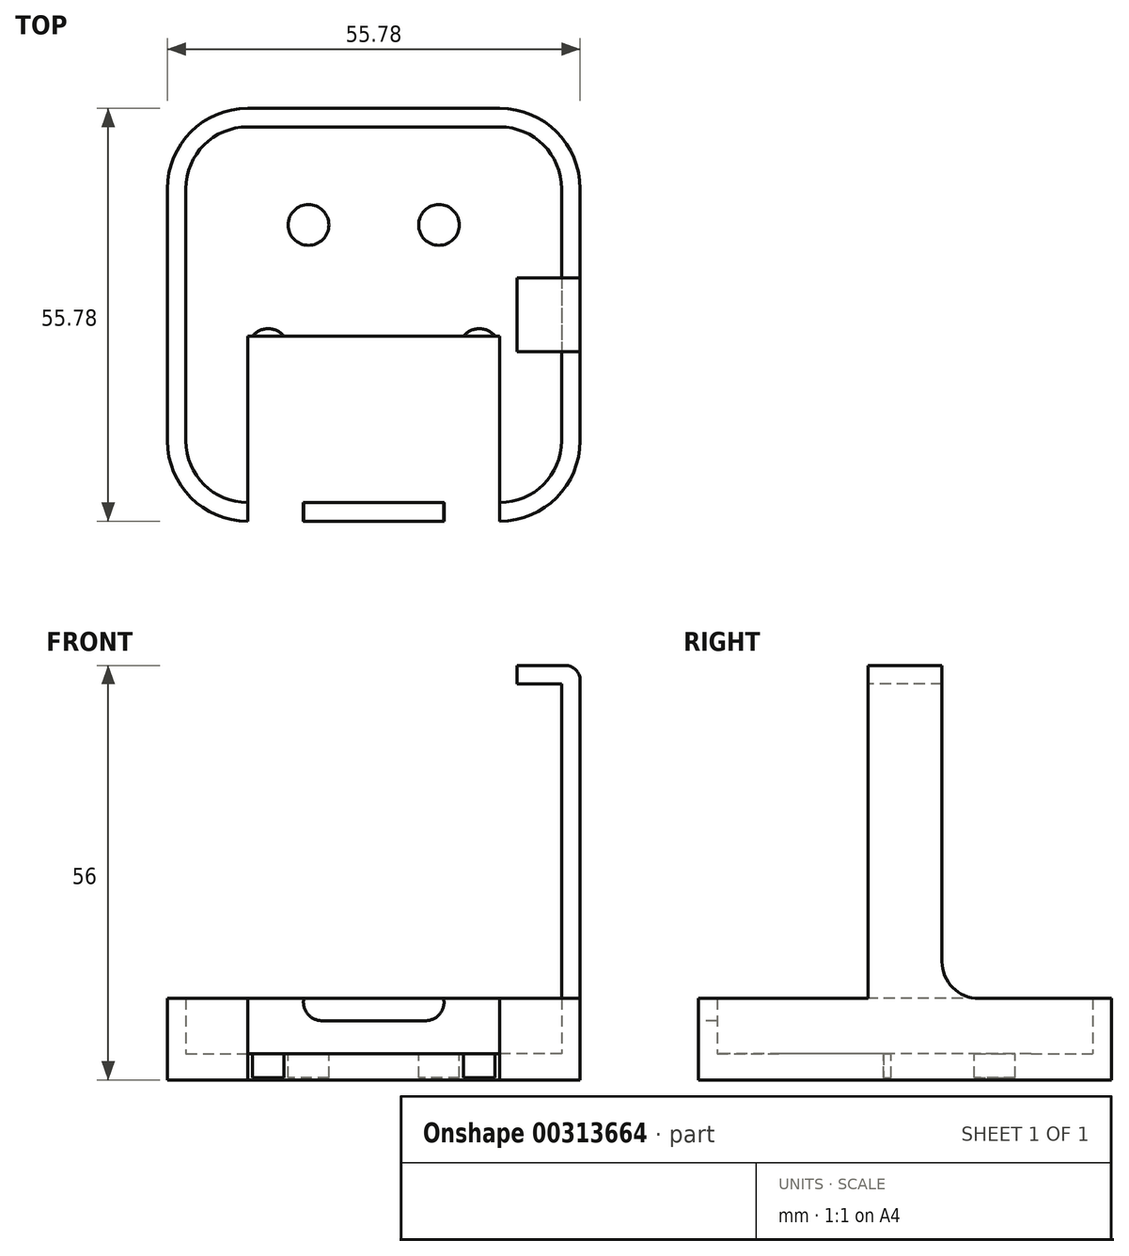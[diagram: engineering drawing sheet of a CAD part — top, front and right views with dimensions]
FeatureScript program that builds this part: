
annotation { "Feature Type Name" : "Feature", "Feature Type Description" : "" }
export const myFeature = defineFeature(function(context is Context, id is Id, definition is map)
    precondition{}
    {
        {
            var Q0;
            Q0=qCreatedBy(makeId("Top.planeOp"),FACE);
            var sketch = newSketch(context, id + "F0", { "sketchPlane" : qUnion([Q0])});
            skLineSegment(sketch, "E0.bottom", {"start": v(17.03, 25.04) * mm, "end": v(-17.03, 25.04) * mm, "construction": true});
            skLineSegment(sketch, "E0.top", {"start": v(17.03, -25.04) * mm, "end": v(-17.03, -25.04) * mm, "construction": true});
            skLineSegment(sketch, "E0.left", {"start": v(25.04, 17.03) * mm, "end": v(25.04, -17.03) * mm, "construction": true});
            skLineSegment(sketch, "E0.right", {"start": v(-25.04, 17.03) * mm, "end": v(-25.04, -17.03) * mm, "construction": true});
            skPoint(sketch, "E0.middle", {"position": v(0, 0) * mm});
            skPoint(sketch, "E1.visualSharp", {"position": v(-25.04, 25.03) * mm});
            skArc(sketch, "E1.filletArc", {"start": v(-17.04, 25.04) * mm, "mid": v(-22.7, 22.7) * mm, "end": v(-25.04, 17.04) * mm, "construction": true});
            skPoint(sketch, "E2.visualSharp", {"position": v(25.03, 25.04) * mm});
            skArc(sketch, "E2.filletArc", {"start": v(25.04, 17.03) * mm, "mid": v(22.7, 22.7) * mm, "end": v(17.03, 25.04) * mm, "construction": true});
            skPoint(sketch, "E3.visualSharp", {"position": v(25.04, -25.03) * mm});
            skArc(sketch, "E3.filletArc", {"start": v(17.03, -25.04) * mm, "mid": v(22.7, -22.7) * mm, "end": v(25.04, -17.03) * mm, "construction": true});
            skPoint(sketch, "E4.visualSharp", {"position": v(-25.03, -25.04) * mm});
            skArc(sketch, "E4.filletArc", {"start": v(-25.04, -17.03) * mm, "mid": v(-22.7, -22.7) * mm, "end": v(-17.03, -25.04) * mm, "construction": true});
            skLineSegment(sketch, "E5.0", {"start": v(17.03, 25.39) * mm, "end": v(-17.04, 25.39) * mm});
            skArc(sketch, "E5.1", {"start": v(25.39, 17.04) * mm, "mid": v(22.94, 22.94) * mm, "end": v(17.03, 25.39) * mm});
            skArc(sketch, "E5.2", {"start": v(-17.04, 25.39) * mm, "mid": v(-22.94, 22.94) * mm, "end": v(-25.39, 17.04) * mm});
            skLineSegment(sketch, "E5.3", {"start": v(25.38, 17.04) * mm, "end": v(25.38, -17.04) * mm});
            skLineSegment(sketch, "E5.4", {"start": v(-25.39, 17.04) * mm, "end": v(-25.38, -17.04) * mm});
            skArc(sketch, "E5.5", {"start": v(-25.39, -17.04) * mm, "mid": v(-22.94, -22.94) * mm, "end": v(-17.03, -25.39) * mm});
            skLineSegment(sketch, "E5.6", {"start": v(17.03, -25.39) * mm, "end": v(-17.03, -25.39) * mm});
            skArc(sketch, "E5.7", {"start": v(17.03, -25.39) * mm, "mid": v(22.94, -22.94) * mm, "end": v(25.39, -17.04) * mm});
            skLineSegment(sketch, "E6.0", {"start": v(17.03, 27.89) * mm, "end": v(-17.04, 27.89) * mm});
            skArc(sketch, "E6.1", {"start": v(27.89, 17.04) * mm, "mid": v(24.7, 24.7) * mm, "end": v(17.03, 27.89) * mm});
            skArc(sketch, "E6.2", {"start": v(-17.04, 27.89) * mm, "mid": v(-24.7, 24.7) * mm, "end": v(-27.89, 17.03) * mm});
            skLineSegment(sketch, "E6.3", {"start": v(27.88, 17.04) * mm, "end": v(27.88, -17.03) * mm});
            skLineSegment(sketch, "E6.4", {"start": v(-27.89, 17.03) * mm, "end": v(-27.88, -17.04) * mm});
            skArc(sketch, "E6.5", {"start": v(-27.89, -17.04) * mm, "mid": v(-24.7, -24.7) * mm, "end": v(-17.03, -27.89) * mm});
            skLineSegment(sketch, "E6.6", {"start": v(17.03, -27.89) * mm, "end": v(-17.03, -27.89) * mm});
            skArc(sketch, "E6.7", {"start": v(17.03, -27.89) * mm, "mid": v(24.7, -24.7) * mm, "end": v(27.89, -17.03) * mm});
            skSolve(sketch);
        }
        {
            var Q0;
            Q0=makeQuery(id+"F0.imprint","IMPRINT",FACE,{"disambiguationData":[TD([[makeQuery(id+"F0.imprint","IMPRINT",EDGE,{"derivedFrom":sQuery(id+"F0.wireOp",EDGE,"E5.0")}),1.0]])]});
            extrude(context, id + "F1", {"entities" : qUnion([Q0]), "depth" : 3.5 * mm});
        }
        {
            var Q0;
            Q0=makeQuery(id+"F0.imprint","IMPRINT",FACE,{"disambiguationData":[TD([[makeQuery(id+"F0.imprint","IMPRINT",EDGE,{"derivedFrom":sQuery(id+"F0.wireOp",EDGE,"E5.0")}),-1.0]])]});
            extrude(context, id + "F2", {"entities" : qUnion([Q0]), "operationType" : NewBodyOperationType.ADD, "depth" : 11 * mm});
        }
        {
            var Q0;
            Q0=makeQuery(id+"F2.opExtrude","SWEPT_FACE",FACE,{"disambiguationData":[OSD([sQuery(id+"F0.wireOp",EDGE,"E6.6")])]});
            var sketch = newSketch(context, id + "F3", { "sketchPlane" : qUnion([Q0])});
            skLineSegment(sketch, "E7.0", {"start": v(17.03, 11) * mm, "end": v(-17.03, 11) * mm, "construction": true});
            skPoint(sketch, "E8.startSnap0", {"position": v(0, 10.5) * mm});
            skArc(sketch, "E9.0.startCap", {"start": v(-7, 8) * mm, "mid": v(-9.5, 10.5) * mm, "end": v(-7, 13) * mm});
            skArc(sketch, "E9.0.endCap", {"start": v(7, 13) * mm, "mid": v(9.5, 10.5) * mm, "end": v(7, 8) * mm});
            skLineSegment(sketch, "E9.0.left", {"start": v(-7, 13) * mm, "end": v(7, 13) * mm});
            skLineSegment(sketch, "E9.0.right", {"start": v(-7, 8) * mm, "end": v(7, 8) * mm});
            skLineSegment(sketch, "E10", {"start": v(0, 11) * mm, "end": v(0, 0) * mm, "construction": true});
            skLineSegment(sketch, "E11.0", {"start": v(17.03, 3.5) * mm, "end": v(-17.03, 3.5) * mm, "construction": true});
            skLineSegment(sketch, "E12", {"start": v(7, 10.5) * mm, "end": v(-7, 10.5) * mm, "construction": true});
            skSolve(sketch);
        }
        {
            var Q0;
            Q0=makeQuery(id+"F3.imprint","IMPRINT",FACE,{"disambiguationData":[TD([[makeQuery(id+"F3.imprint","IMPRINT",EDGE,{"derivedFrom":sQuery(id+"F3.wireOp",EDGE,"E9.0.startCap")}),-1.0]])]});
            extrude(context, id + "F4", {"entities" : qUnion([Q0]), "operationType" : NewBodyOperationType.REMOVE, "oppositeDirection" : true, "depth" : 25 * mm});
        }
        {
            var Q0;
            Q0=makeQuery(id+"F2.opExtrude","CAP_FACE",FACE,{"disambiguationData":[OSD([sQuery(id+"F0.wireOp",EDGE,"E5.0"),sQuery(id+"F0.wireOp",EDGE,"E5.1"),sQuery(id+"F0.wireOp",EDGE,"E5.2"),sQuery(id+"F0.wireOp",EDGE,"E5.3"),sQuery(id+"F0.wireOp",EDGE,"E5.4"),sQuery(id+"F0.wireOp",EDGE,"E5.5"),sQuery(id+"F0.wireOp",EDGE,"E5.6"),sQuery(id+"F0.wireOp",EDGE,"E5.7"),sQuery(id+"F0.wireOp",EDGE,"E6.0"),sQuery(id+"F0.wireOp",EDGE,"E6.1"),sQuery(id+"F0.wireOp",EDGE,"E6.2"),sQuery(id+"F0.wireOp",EDGE,"E6.3"),sQuery(id+"F0.wireOp",EDGE,"E6.4"),sQuery(id+"F0.wireOp",EDGE,"E6.5"),sQuery(id+"F0.wireOp",EDGE,"E6.6"),sQuery(id+"F0.wireOp",EDGE,"E6.7")])],"isStart":false});
            var sketch = newSketch(context, id + "F5", { "sketchPlane" : qUnion([Q0])});
            skPoint(sketch, "E13", {"position": v(-27.89, 0) * mm});
            skPoint(sketch, "E14", {"position": v(-25.39, 0) * mm});
            skPoint(sketch, "E15", {"position": v(25.38, 0) * mm});
            skPoint(sketch, "E16", {"position": v(27.88, 0) * mm});
            skLineSegment(sketch, "E17", {"start": v(25.38, 0) * mm, "end": v(27.88, 0) * mm, "construction": true});
            skLineSegment(sketch, "E18", {"start": v(-25.39, 0) * mm, "end": v(-27.89, 0) * mm, "construction": true});
            skPoint(sketch, "E19", {"position": v(-26.63, 0) * mm});
            skPoint(sketch, "E20", {"position": v(26.63, 0) * mm});
            skLineSegment(sketch, "E21", {"start": v(0, 27.89) * mm, "end": v(0, 25.39) * mm, "construction": true});
            skPoint(sketch, "E22", {"position": v(0, 26.63) * mm});
            skLineSegment(sketch, "E23.bottom", {"start": v(25.38, -5) * mm, "end": v(27.88, -5) * mm});
            skLineSegment(sketch, "E23.top", {"start": v(25.38, 5) * mm, "end": v(27.88, 5) * mm});
            skLineSegment(sketch, "E23.left", {"start": v(25.38, -5) * mm, "end": v(25.38, 5) * mm});
            skLineSegment(sketch, "E23.right", {"start": v(27.88, -5) * mm, "end": v(27.88, 5) * mm});
            skSolve(sketch);
        }
        {
            var Q0;
            Q0=makeQuery(id+"F5.imprint","IMPRINT",FACE,{"disambiguationData":[TD([[makeQuery(id+"F5.imprint","IMPRINT",EDGE,{"derivedFrom":sQuery(id+"F5.wireOp",EDGE,"E23.bottom")}),1.0]])]});
            extrude(context, id + "F6", {"entities" : qUnion([Q0]), "operationType" : NewBodyOperationType.ADD, "depth" : (50 - 7.5) * mm});
        }
        {
            var Q0;
            Q0=makeQuery(id+"F6.opExtrude","CAP_FACE",FACE,{"disambiguationData":[OSD([sQuery(id+"F5.wireOp",EDGE,"E23.bottom"),sQuery(id+"F5.wireOp",EDGE,"E23.top"),sQuery(id+"F5.wireOp",EDGE,"E23.left"),sQuery(id+"F5.wireOp",EDGE,"E23.right")])],"isStart":false});
            var sketch = newSketch(context, id + "F7", { "sketchPlane" : qUnion([Q0])});
            skLineSegment(sketch, "E24.bottom", {"start": v(27.88, -5) * mm, "end": v(19.38, -5) * mm});
            skLineSegment(sketch, "E24.top", {"start": v(27.88, 5) * mm, "end": v(19.38, 5) * mm});
            skLineSegment(sketch, "E24.left", {"start": v(27.88, -5) * mm, "end": v(27.88, 5) * mm});
            skLineSegment(sketch, "E24.right", {"start": v(19.38, -5) * mm, "end": v(19.38, 5) * mm});
            skSolve(sketch);
        }
        {
            var Q0;
            {var subQ2=sQuery(id+"F7.wireOp",EDGE,"E24.left");Q0=makeQuery(id+"F7.imprint","IMPRINT",FACE,{"disambiguationData":[TD([[makeQuery(id+"F7.imprint","IMPRINT",EDGE,{"derivedFrom":subQ2}),-1.0]])]});}
            var Q1;
            {var subQ2=sQuery(id+"F7.wireOp",EDGE,"E24.right");Q1=makeQuery(id+"F7.imprint","IMPRINT",FACE,{"disambiguationData":[TD([[makeQuery(id+"F7.imprint","IMPRINT",EDGE,{"derivedFrom":subQ2}),-1.0]])]});}
            extrude(context, id + "F8", {"entities" : qUnion([Q0, Q1]), "operationType" : NewBodyOperationType.ADD, "depth" : 2.5 * mm});
        }
        {
            var Q0;
            Q0=makeQuery(id+"F6.opExtrude","CAP_EDGE",EDGE,{"disambiguationData":[OSD([sQuery(id+"F5.wireOp",EDGE,"E23.left")])],"isStart":false});
            var Q1;
            Q1=makeQuery(id+"F8.opExtrude","CAP_EDGE",EDGE,{"disambiguationData":[OSD([sQuery(id+"F7.wireOp",EDGE,"E24.left")])],"isStart":false});
            fillet(context, id + "F9", {"entities" : qUnion([Q0, Q1]), "radius" : 2 * mm, "tangentPropagation" : true, "allowEdgeOverflow" : false});
        }
        {
            var Q0;
            Q0=makeQuery(id+"F6.opExtrude","CAP_EDGE",EDGE,{"disambiguationData":[OSD([sQuery(id+"F5.wireOp",EDGE,"E23.top")])],"isStart":true});
            var Q1;
            Q1=makeQuery(id+"F6.opExtrude","CAP_EDGE",EDGE,{"disambiguationData":[OSD([sQuery(id+"F5.wireOp",EDGE,"E23.bottom")])],"isStart":true});
            fillet(context, id + "F10", {"entities" : qUnion([Q0, Q1]), "radius" : 5 * mm, "tangentPropagation" : true, "allowEdgeOverflow" : false});
        }
        {
            var Q0;
            Q0=makeQuery(id+"F1.opExtrude","CAP_FACE",FACE,{"disambiguationData":[OSD([sQuery(id+"F0.wireOp",EDGE,"E5.0"),sQuery(id+"F0.wireOp",EDGE,"E5.1"),sQuery(id+"F0.wireOp",EDGE,"E5.2"),sQuery(id+"F0.wireOp",EDGE,"E5.3"),sQuery(id+"F0.wireOp",EDGE,"E5.4"),sQuery(id+"F0.wireOp",EDGE,"E5.5"),sQuery(id+"F0.wireOp",EDGE,"E5.6"),sQuery(id+"F0.wireOp",EDGE,"E5.7")])],"isStart":false});
            var sketch = newSketch(context, id + "F11", { "sketchPlane" : qUnion([Q0])});
            skCircle(sketch, "E25", {"center": v(0, -15) * mm, "radius": 2.75 * mm});
            skCircle(sketch, "E26.1.0", {"center": v(14.27, -4.64) * mm, "radius": 2.75 * mm});
            skCircle(sketch, "E26.2.0", {"center": v(8.82, 12.14) * mm, "radius": 2.75 * mm});
            skPoint(sketch, "E26.center", {"position": v(0, 0) * mm});
            skCircle(sketch, "E27.1.3.0", {"center": v(-8.82, 12.14) * mm, "radius": 2.75 * mm});
            skCircle(sketch, "E27.1.4.0", {"center": v(-14.27, -4.64) * mm, "radius": 2.75 * mm});
            skSolve(sketch);
        }
        {
            var Q0;
            Q0 = qSketchRegion(id + "F11", true);
            extrude(context, id + "F12", {"entities" : qUnion([Q0]), "operationType" : NewBodyOperationType.REMOVE, "oppositeDirection" : true, "depth" : 3.2 * mm});
        }
    });
